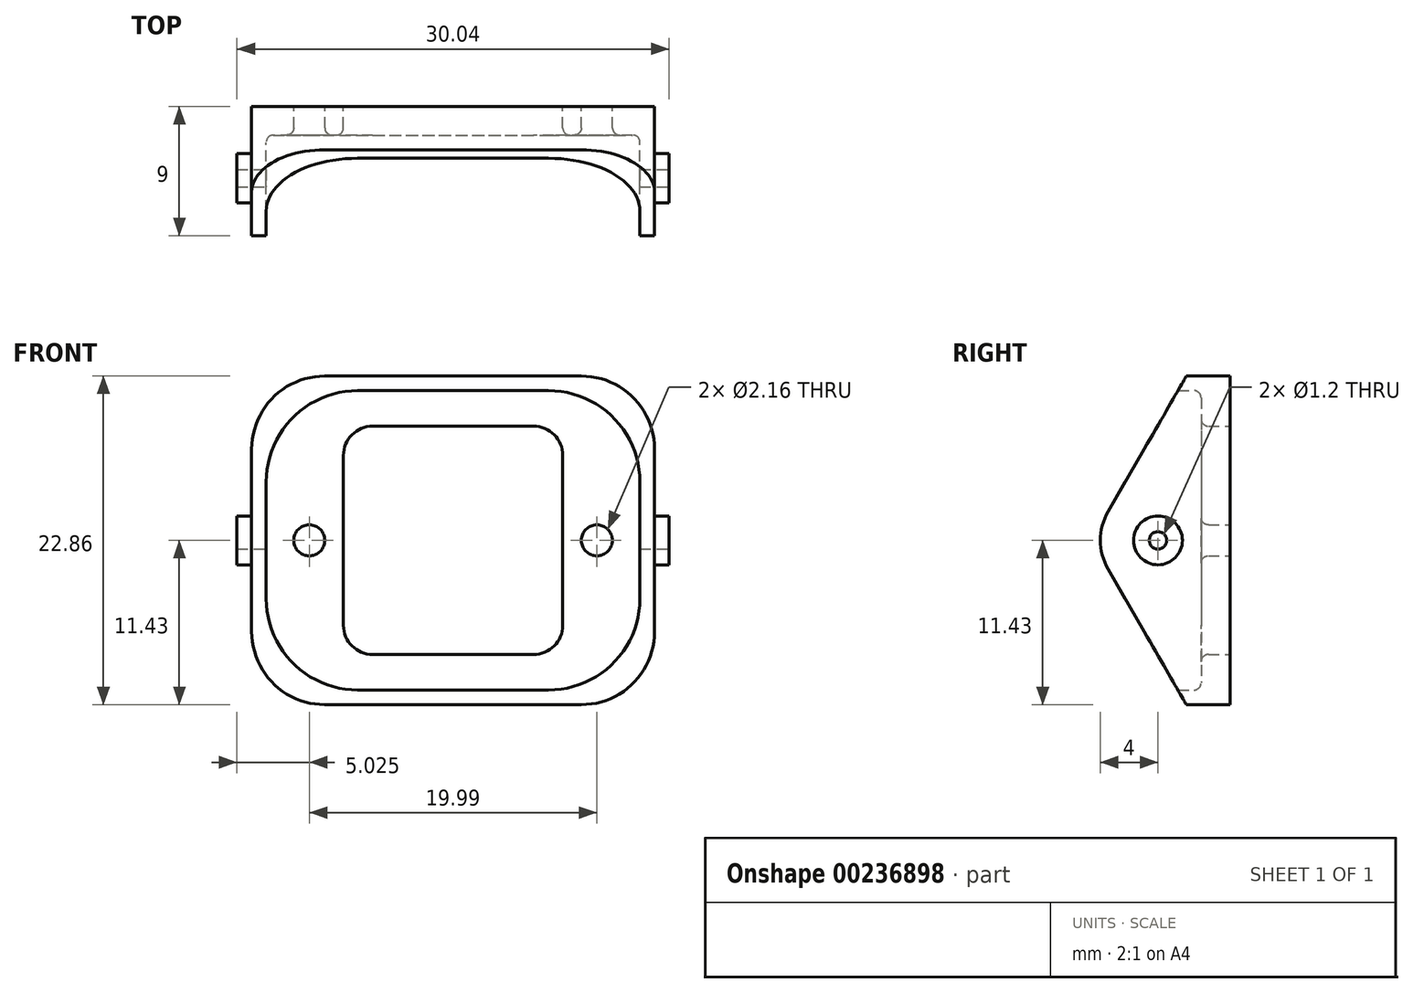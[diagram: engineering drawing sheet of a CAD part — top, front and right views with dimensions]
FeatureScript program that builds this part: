
annotation { "Feature Type Name" : "Feature", "Feature Type Description" : "" }
export const myFeature = defineFeature(function(context is Context, id is Id, definition is map)
    precondition{}
    {
        {
            var Q0;
            Q0=qCreatedBy(makeId("Front.planeOp"),FACE);
            var sketch = newSketch(context, id + "F0", { "sketchPlane" : qUnion([Q0])});
            skLineSegment(sketch, "E0.bottom", {"start": v(-8.92, 11.43) * mm, "end": v(8.92, 11.43) * mm});
            skLineSegment(sketch, "E0.top", {"start": v(-8.92, -11.43) * mm, "end": v(8.92, -11.43) * mm});
            skLineSegment(sketch, "E0.left", {"start": v(-14, 6.35) * mm, "end": v(-14, -6.35) * mm});
            skLineSegment(sketch, "E0.right", {"start": v(14, 6.35) * mm, "end": v(14, -6.35) * mm});
            skPoint(sketch, "E0.middle", {"position": v(0, 0) * mm});
            skLineSegment(sketch, "E1.bottom", {"start": v(-5.59, 7.94) * mm, "end": v(5.59, 7.94) * mm});
            skLineSegment(sketch, "E1.top", {"start": v(-5.59, -7.94) * mm, "end": v(5.59, -7.94) * mm});
            skLineSegment(sketch, "E1.left", {"start": v(-7.62, 5.9) * mm, "end": v(-7.62, -5.9) * mm});
            skLineSegment(sketch, "E1.right", {"start": v(7.62, 5.9) * mm, "end": v(7.62, -5.9) * mm});
            skCircle(sketch, "E2", {"center": v(0, 0) * mm, "radius": 10 * mm, "construction": true});
            skCircle(sketch, "E3", {"center": v(-10, 0) * mm, "radius": 1.08 * mm});
            skCircle(sketch, "E4", {"center": v(10, 0) * mm, "radius": 1.08 * mm});
            skPoint(sketch, "E4.centerSnap0", {"position": v(7.62, 0) * mm});
            skPoint(sketch, "E5.visualSharp", {"position": v(-7.62, 7.94) * mm});
            skArc(sketch, "E5.filletArc", {"start": v(-5.59, 7.94) * mm, "mid": v(-7.02, 7.34) * mm, "end": v(-7.62, 5.9) * mm});
            skPoint(sketch, "E6.visualSharp", {"position": v(7.62, 7.94) * mm});
            skArc(sketch, "E6.filletArc", {"start": v(7.62, 5.9) * mm, "mid": v(7.02, 7.34) * mm, "end": v(5.59, 7.94) * mm});
            skPoint(sketch, "E7.visualSharp", {"position": v(7.62, -7.94) * mm});
            skArc(sketch, "E7.filletArc", {"start": v(5.59, -7.94) * mm, "mid": v(7.02, -7.34) * mm, "end": v(7.62, -5.9) * mm});
            skPoint(sketch, "E8.visualSharp", {"position": v(-7.62, -7.94) * mm});
            skArc(sketch, "E8.filletArc", {"start": v(-7.62, -5.9) * mm, "mid": v(-7.02, -7.34) * mm, "end": v(-5.59, -7.94) * mm});
            skPoint(sketch, "E9.visualSharp", {"position": v(-14, 11.43) * mm});
            skArc(sketch, "E9.filletArc", {"start": v(-8.92, 11.43) * mm, "mid": v(-12.51, 9.94) * mm, "end": v(-14, 6.35) * mm});
            skPoint(sketch, "E10.visualSharp", {"position": v(-14, -11.43) * mm});
            skArc(sketch, "E10.filletArc", {"start": v(-14, -6.35) * mm, "mid": v(-12.51, -9.94) * mm, "end": v(-8.92, -11.43) * mm});
            skPoint(sketch, "E11.visualSharp", {"position": v(14, -11.43) * mm});
            skArc(sketch, "E11.filletArc", {"start": v(8.92, -11.43) * mm, "mid": v(12.51, -9.94) * mm, "end": v(14, -6.35) * mm});
            skPoint(sketch, "E12.visualSharp", {"position": v(14, 11.43) * mm});
            skArc(sketch, "E12.filletArc", {"start": v(14, 6.35) * mm, "mid": v(12.51, 9.94) * mm, "end": v(8.92, 11.43) * mm});
            skSolve(sketch);
        }
        {
            var Q0;
            Q0=qSketchRegion(id+"F0",true);
            extrude(context, id + "F1", {"entities" : qUnion([Q0]), "depth" : 2 * mm});
        }
        {
            var Q0;
            Q0=makeQuery(id+"F1.opExtrude","CAP_FACE",FACE,{"disambiguationData":[OSD([sQuery(id+"F0.wireOp",EDGE,"E0.bottom"),sQuery(id+"F0.wireOp",EDGE,"E0.top"),sQuery(id+"F0.wireOp",EDGE,"E0.left"),sQuery(id+"F0.wireOp",EDGE,"E0.right"),sQuery(id+"F0.wireOp",EDGE,"E1.bottom"),sQuery(id+"F0.wireOp",EDGE,"E1.top"),sQuery(id+"F0.wireOp",EDGE,"E1.left"),sQuery(id+"F0.wireOp",EDGE,"E1.right"),sQuery(id+"F0.wireOp",EDGE,"E3"),sQuery(id+"F0.wireOp",EDGE,"E4"),sQuery(id+"F0.wireOp",EDGE,"E5.filletArc"),sQuery(id+"F0.wireOp",EDGE,"E6.filletArc"),sQuery(id+"F0.wireOp",EDGE,"E7.filletArc"),sQuery(id+"F0.wireOp",EDGE,"E8.filletArc"),sQuery(id+"F0.wireOp",EDGE,"E9.filletArc"),sQuery(id+"F0.wireOp",EDGE,"E10.filletArc"),sQuery(id+"F0.wireOp",EDGE,"E11.filletArc"),sQuery(id+"F0.wireOp",EDGE,"E12.filletArc")])],"isStart":false});
            var sketch = newSketch(context, id + "F2", { "sketchPlane" : qUnion([Q0])});
            skLineSegment(sketch, "E13.0", {"start": v(-8.92, 11.43) * mm, "end": v(8.92, 11.43) * mm});
            skLineSegment(sketch, "E14.0", {"start": v(-14, 6.35) * mm, "end": v(-14, -6.35) * mm});
            skPoint(sketch, "E14.1", {"position": v(-12.51, 9.94) * mm});
            skArc(sketch, "E15.0", {"start": v(-8.92, 11.43) * mm, "mid": v(-12.51, 9.94) * mm, "end": v(-14, 6.35) * mm});
            skArc(sketch, "E16.0", {"start": v(14, 6.35) * mm, "mid": v(12.51, 9.94) * mm, "end": v(8.92, 11.43) * mm});
            skLineSegment(sketch, "E17.0", {"start": v(14, 6.35) * mm, "end": v(14, -6.35) * mm});
            skArc(sketch, "E18.0", {"start": v(8.92, -11.43) * mm, "mid": v(12.51, -9.94) * mm, "end": v(14, -6.35) * mm});
            skLineSegment(sketch, "E19.0", {"start": v(-8.92, -11.43) * mm, "end": v(8.92, -11.43) * mm});
            skArc(sketch, "E20.0", {"start": v(-14, -6.35) * mm, "mid": v(-12.51, -9.94) * mm, "end": v(-8.92, -11.43) * mm});
            skLineSegment(sketch, "E21.0", {"start": v(-6.64, 10.41) * mm, "end": v(6.64, 10.41) * mm});
            skLineSegment(sketch, "E22.0", {"start": v(12.99, 4.06) * mm, "end": v(12.99, -4.06) * mm});
            skLineSegment(sketch, "E23.0", {"start": v(-12.99, 4.06) * mm, "end": v(-12.99, -4.06) * mm});
            skLineSegment(sketch, "E24.0", {"start": v(-6.64, -10.41) * mm, "end": v(6.64, -10.41) * mm});
            skPoint(sketch, "E25.visualSharp", {"position": v(-12.99, 10.41) * mm});
            skArc(sketch, "E25.filletArc", {"start": v(-6.64, 10.41) * mm, "mid": v(-11.13, 8.55) * mm, "end": v(-12.99, 4.06) * mm});
            skPoint(sketch, "E26.visualSharp", {"position": v(-12.99, -10.41) * mm});
            skArc(sketch, "E26.filletArc", {"start": v(-12.99, -4.06) * mm, "mid": v(-11.13, -8.55) * mm, "end": v(-6.64, -10.41) * mm});
            skPoint(sketch, "E27.visualSharp", {"position": v(12.99, -10.41) * mm});
            skArc(sketch, "E27.filletArc", {"start": v(6.64, -10.41) * mm, "mid": v(11.13, -8.55) * mm, "end": v(12.99, -4.06) * mm});
            skPoint(sketch, "E28.visualSharp", {"position": v(12.99, 10.41) * mm});
            skArc(sketch, "E28.filletArc", {"start": v(12.99, 4.06) * mm, "mid": v(11.13, 8.55) * mm, "end": v(6.64, 10.41) * mm});
            skSolve(sketch);
        }
        {
            var Q0;
            Q0=qSketchRegion(id+"F2",true);
            extrude(context, id + "F3", {"entities" : qUnion([Q0]), "operationType" : NewBodyOperationType.ADD, "depth" : 19.99 * mm});
        }
        {
            var Q0;
            Q0=makeQuery(id+"F1.opExtrude","CAP_FACE",FACE,{"disambiguationData":[OSD([sQuery(id+"F0.wireOp",EDGE,"E0.bottom"),sQuery(id+"F0.wireOp",EDGE,"E0.top"),sQuery(id+"F0.wireOp",EDGE,"E0.left"),sQuery(id+"F0.wireOp",EDGE,"E0.right"),sQuery(id+"F0.wireOp",EDGE,"E1.bottom"),sQuery(id+"F0.wireOp",EDGE,"E1.top"),sQuery(id+"F0.wireOp",EDGE,"E1.left"),sQuery(id+"F0.wireOp",EDGE,"E1.right"),sQuery(id+"F0.wireOp",EDGE,"E3"),sQuery(id+"F0.wireOp",EDGE,"E4"),sQuery(id+"F0.wireOp",EDGE,"E5.filletArc"),sQuery(id+"F0.wireOp",EDGE,"E6.filletArc"),sQuery(id+"F0.wireOp",EDGE,"E7.filletArc"),sQuery(id+"F0.wireOp",EDGE,"E8.filletArc"),sQuery(id+"F0.wireOp",EDGE,"E9.filletArc"),sQuery(id+"F0.wireOp",EDGE,"E10.filletArc"),sQuery(id+"F0.wireOp",EDGE,"E11.filletArc"),sQuery(id+"F0.wireOp",EDGE,"E12.filletArc")])],"isStart":false});
            fillet(context, id + "F4", {"entities" : qUnion([Q0]), "radius" : 0.5 * mm, "tangentPropagation" : true, "allowEdgeOverflow" : false});
        }
        {
            var Q0;
            Q0=makeQuery(id+"F3.boolean.opBoolean","MERGE",FACE,{"derivedFrom":[makeQuery(id+"F1.opExtrude","SWEPT_FACE",FACE,{"disambiguationData":[OSD([sQuery(id+"F0.wireOp",EDGE,"E0.right")])]}),makeQuery(id+"F3.opExtrude","SWEPT_FACE",FACE,{"disambiguationData":[OSD([sQuery(id+"F2.wireOp",EDGE,"E17.0")])]})]});
            var sketch = newSketch(context, id + "F5", { "sketchPlane" : qUnion([Q0])});
            skLineSegment(sketch, "E29", {"start": v(0, 0) * mm, "end": v(-21.48, 0) * mm, "construction": true});
            skCircle(sketch, "E30", {"center": v(-5, 0) * mm, "radius": 0.6 * mm});
            skCircle(sketch, "E31", {"center": v(-11, 0) * mm, "radius": 0.6 * mm});
            skSolve(sketch);
        }
        {
            var Q0;
            Q0=qSketchRegion(id+"F5",true);
            extrude(context, id + "F6", {"entities" : qUnion([Q0]), "operationType" : NewBodyOperationType.REMOVE, "endBound" : BoundingType.THROUGH_ALL, "oppositeDirection" : true, "depth" : 25.4 * mm});
        }
        {
            var Q0;
            Q0=makeQuery(id+"F3.boolean.opBoolean","MERGE",FACE,{"derivedFrom":[makeQuery(id+"F1.opExtrude","SWEPT_FACE",FACE,{"disambiguationData":[OSD([sQuery(id+"F0.wireOp",EDGE,"E0.right")])]}),makeQuery(id+"F3.opExtrude","SWEPT_FACE",FACE,{"disambiguationData":[OSD([sQuery(id+"F2.wireOp",EDGE,"E17.0")])]})]});
            var sketch = newSketch(context, id + "F7", { "sketchPlane" : qUnion([Q0])});
            skCircle(sketch, "E32", {"center": v(-5, 0) * mm, "radius": 1.7 * mm});
            skCircle(sketch, "E33", {"center": v(-11, 0) * mm, "radius": 1.7 * mm});
            skCircle(sketch, "E34.0", {"center": v(-11, 0) * mm, "radius": 0.6 * mm});
            skCircle(sketch, "E35.0", {"center": v(-5, 0) * mm, "radius": 0.6 * mm});
            skSolve(sketch);
        }
        {
            var Q0;
            Q0=qSketchRegion(id+"F7",true);
            extrude(context, id + "F8", {"entities" : qUnion([Q0]), "operationType" : NewBodyOperationType.ADD, "depth" : 1.02 * mm});
        }
        {
            var Q0;
            Q0=makeQuery(id+"F3.boolean.opBoolean","MERGE",FACE,{"derivedFrom":[makeQuery(id+"F1.opExtrude","SWEPT_FACE",FACE,{"disambiguationData":[OSD([sQuery(id+"F0.wireOp",EDGE,"E0.left")])]}),makeQuery(id+"F3.opExtrude","SWEPT_FACE",FACE,{"disambiguationData":[OSD([sQuery(id+"F2.wireOp",EDGE,"E14.0")])]})]});
            var sketch = newSketch(context, id + "F9", { "sketchPlane" : qUnion([Q0])});
            skCircle(sketch, "E36", {"center": v(11, 0) * mm, "radius": 1.7 * mm});
            skCircle(sketch, "E37", {"center": v(5, 0) * mm, "radius": 1.7 * mm});
            skCircle(sketch, "E38.0", {"center": v(11, 0) * mm, "radius": 0.6 * mm});
            skCircle(sketch, "E39.0", {"center": v(5, 0) * mm, "radius": 0.6 * mm});
            skSolve(sketch);
        }
        {
            var Q0;
            Q0=qSketchRegion(id+"F9",true);
            extrude(context, id + "F10", {"entities" : qUnion([Q0]), "operationType" : NewBodyOperationType.ADD, "depth" : 1.02 * mm});
        }
        {
            var Q0;
            Q0=qCreatedBy(makeId("Right.planeOp"),FACE);
            var sketch = newSketch(context, id + "F11", { "sketchPlane" : qUnion([Q0])});
            skLineSegment(sketch, "E40", {"start": v(-8.46, 2) * mm, "end": v(-2.29, 12.7) * mm});
            skLineSegment(sketch, "E41", {"start": v(-2.29, 12.7) * mm, "end": v(-49.95, 19.9) * mm});
            skLineSegment(sketch, "E42", {"start": v(-49.95, 19.9) * mm, "end": v(-49.95, -23.94) * mm});
            skLineSegment(sketch, "E43", {"start": v(-49.95, -23.94) * mm, "end": v(4.2, -23.94) * mm});
            skLineSegment(sketch, "E44", {"start": v(4.2, -23.94) * mm, "end": v(-8.46, -2) * mm});
            skArc(sketch, "E45", {"start": v(-8.46, 2) * mm, "mid": v(-9, 0) * mm, "end": v(-8.46, -2) * mm});
            skSolve(sketch);
        }
        {
            var Q0;
            Q0 = qSketchRegion(id + "F11", true);
            extrude(context, id + "F12", {"entities" : qUnion([Q0]), "operationType" : NewBodyOperationType.REMOVE, "oppositeDirection" : true, "depth" : 25.4 * mm, "hasSecondDirection" : true, "secondDirectionOppositeDirection" : false, "secondDirectionDepth" : 25.4 * mm});
        }
    });
